# Revit family: Skyfold_Mirage-Partition-10_Panels_High-15-2_to_18-10_FC_4625_to_5740
name_source: partatom
category: Generic Models
units: mm (PartAtom-declared; Revit-internal decimal feet)

## family parameters
Always vertical = Yes
Can host rebar = No
Cut with Voids When Loaded = No
Host = Ceiling
Maintain Annotation Orientation = No
Part Type = Normal
Room Calculation Point = No
Round Connector Dimension = Use Diameter
Shared = No

## types (5) — shared parameters
Default Elevation = 0' - 0"
Description = Custom Powerlift Partitions
Distance From Acoustic Barrier = 0' - 2"
Manufacturer = Skyfold
Model = Compact Drive System
URL = http://www.skyfold.com
Wall Thickness = 0' - 11 3/4"

## per-type parameters (varying)
| type | Beam Height"B" | Grid Height"F" | Pocket Height"D" | Pocket Width"E" | Top of Pocket"C" | Total Panel Height |
| 15' - 2" | 19' - 5" | 1' - 9 3/16" | 3' - 0 5/8" | 4' - 1 3/8" | 18' - 2 5/8" | 18' - 0 7/8" |
| 18' - 10" | 23' - 2" | 2' - 1 11/16" | 3' - 1 5/8" | 4' - 10 3/8" | 21' - 11 5/8" | 21' - 9 7/8" |
| 18' - 0" | 22' - 4" | 2' - 0 11/16" | 3' - 1 5/8" | 4' - 8 3/8" | 21' - 1 5/8" | 20' - 11 7/8" |
| 17' - 0" | 21' - 3" | 1' - 11 3/8" | 3' - 0 1/2" | 4' - 5 3/4" | 20' - 0 1/2" | 19' - 10 3/4" |
| 16' - 0" | 20' - 3" | 1' - 10 3/16" | 3' - 0 5/8" | 4' - 3 3/8" | 19' - 0 5/8" | 18' - 10 7/8" |

note: column(s) folded — value = type name in every type: Ceiling Height"A"

## geometry (parser evidence)
native form markers: Sweep x36
no freeform markers — native parametric forms only
